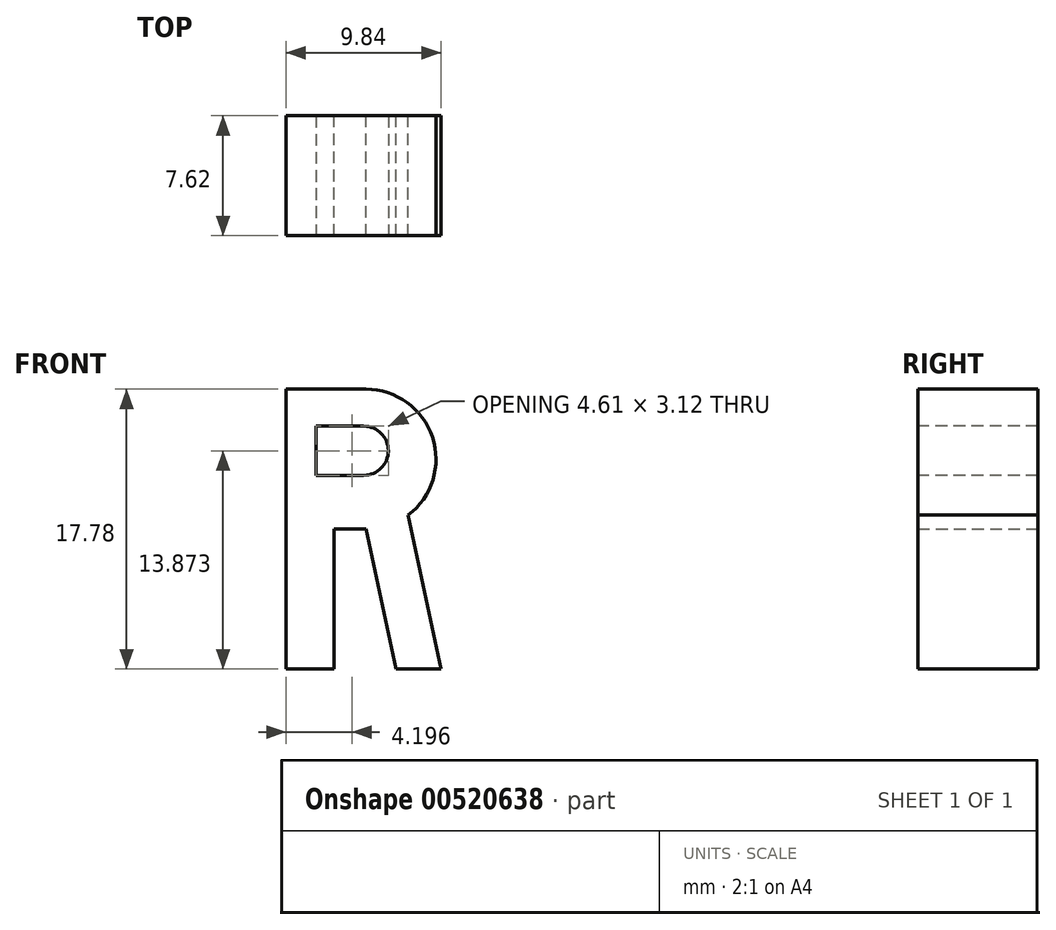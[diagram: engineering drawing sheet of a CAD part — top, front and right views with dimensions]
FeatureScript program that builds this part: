
annotation { "Feature Type Name" : "Feature", "Feature Type Description" : "" }
export const myFeature = defineFeature(function(context is Context, id is Id, definition is map)
    precondition{}
    {
        {
            var Q0;
            Q0=qCreatedBy(makeId("Front.planeOp"),FACE);
            var sketch = newSketch(context, id + "F0", { "sketchPlane" : qUnion([Q0])});
            skLineSegment(sketch, "E0.bottom", {"start": v(-12.04, 8.9) * mm, "end": v(-6.96, 8.9) * mm});
            skLineSegment(sketch, "E0.top", {"start": v(-12.04, 0) * mm, "end": v(-6.96, 0) * mm});
            skLineSegment(sketch, "E0.left", {"start": v(-12.04, 8.89) * mm, "end": v(-12.04, 0) * mm});
            skLineSegment(sketch, "E0.right", {"start": v(-6.96, 8.89) * mm, "end": v(-6.96, 0) * mm});
            skArc(sketch, "E1", {"start": v(-6.96, 0) * mm, "mid": v(-2.51, 4.44) * mm, "end": v(-6.96, 8.89) * mm});
            skLineSegment(sketch, "E2", {"start": v(-12.04, 0) * mm, "end": v(-12.04, -8.89) * mm});
            skLineSegment(sketch, "E3", {"start": v(-12.04, -8.89) * mm, "end": v(-9, -8.89) * mm});
            skLineSegment(sketch, "E4", {"start": v(-9, -8.9) * mm, "end": v(-9, 0) * mm});
            skPoint(sketch, "E5.endSnap0", {"position": v(-2.51, 4.45) * mm});
            skLineSegment(sketch, "E6", {"start": v(-6.96, 0) * mm, "end": v(-5.06, -8.89) * mm});
            skLineSegment(sketch, "E7", {"start": v(-5.06, -8.89) * mm, "end": v(-2.2, -8.89) * mm});
            skLineSegment(sketch, "E8", {"start": v(-2.2, -8.89) * mm, "end": v(-4.28, 0.9) * mm});
            skSolve(sketch);
        }
        {
            var Q0;
            Q0=makeQuery(id+"F0.imprint","IMPRINT",FACE,{"disambiguationData":[TD([[makeQuery(id+"F0.imprint","IMPRINT",EDGE,{"derivedFrom":sQuery(id+"F0.wireOp",EDGE,"E0.bottom")}),-1.0]])]});
            var Q1;
            Q1=makeQuery(id+"F0.imprint","IMPRINT",FACE,{"disambiguationData":[TD([[makeQuery(id+"F0.imprint","IMPRINT",EDGE,{"derivedFrom":sQuery(id+"F0.wireOp",EDGE,"E0.right")}),1.0]])]});
            var Q2;
            {var subQ2=sQuery(id+"F0.wireOp",EDGE,"p5OlRfSF-DRMH-5xbW-HlBg-Sh4KWYqeQvzk");Q2=makeQuery(id+"F0.imprint","IMPRINT",FACE,{"disambiguationData":[TD([[makeQuery(id+"F0.imprint","IMPRINT",EDGE,{"derivedFrom":subQ2}),-1.0]])]});}
            var Q3;
            {var subQ0=sQuery(id+"F0.wireOp",EDGE,"E2");Q3=makeQuery(id+"F0.imprint","IMPRINT",FACE,{"disambiguationData":[TD([[makeQuery(id+"F0.imprint","IMPRINT",EDGE,{"derivedFrom":subQ0}),1.0]])]});}
            extrude(context, id + "F1", {"entities" : qUnion([Q0, Q1, Q2, Q3]), "depth" : 7.62 * mm, "offsetDistance" : 25.4 * mm});
        }
        {
            var Q0;
            Q0 = qSketchRegion(id + "F0", true);
            extrude(context, id + "F2", {"entities" : qUnion([Q0]), "operationType" : NewBodyOperationType.ADD, "depth" : 7.62 * mm, "offsetDistance" : 25.4 * mm});
        }
        {
            var Q0;
            {var subQ0=sQuery(id+"F0.wireOp",EDGE,"E4");var subQ1=sQuery(id+"F0.wireOp",EDGE,"E3");var subQ2=sQuery(id+"F0.wireOp",EDGE,"E2");var subQ3=sQuery(id+"F0.wireOp",EDGE,"E1");var subQ4=sQuery(id+"F0.wireOp",EDGE,"E0.left");var subQ5=sQuery(id+"F0.wireOp",EDGE,"E0.top");var subQ6=sQuery(id+"F0.wireOp",EDGE,"E0.bottom");Q0=makeQuery(id+"F2.boolean.opBoolean","MERGE",FACE,{"derivedFrom":[makeQuery(id+"F1.opExtrude","CAP_FACE",FACE,{"disambiguationData":[OSD([subQ6,subQ5,subQ4,subQ3,subQ2,subQ1,subQ0])],"isStart":false}),makeQuery(id+"F2.opExtrude","CAP_FACE",FACE,{"disambiguationData":[OSD([subQ6,subQ5,subQ4,subQ3,subQ2,subQ1,subQ0,sQuery(id+"F0.wireOp",EDGE,"E6"),sQuery(id+"F0.wireOp",EDGE,"E7"),sQuery(id+"F0.wireOp",EDGE,"E8")])],"isStart":false})]});}
            var sketch = newSketch(context, id + "F3", { "sketchPlane" : qUnion([Q0])});
            skLineSegment(sketch, "E9.bottom", {"start": v(-10.15, 6.54) * mm, "end": v(-7.1, 6.54) * mm});
            skLineSegment(sketch, "E9.top", {"start": v(-10.15, 3.42) * mm, "end": v(-7.1, 3.42) * mm});
            skLineSegment(sketch, "E9.left", {"start": v(-10.15, 6.54) * mm, "end": v(-10.15, 3.42) * mm});
            skLineSegment(sketch, "E9.right", {"start": v(-7.1, 6.54) * mm, "end": v(-7.1, 3.42) * mm});
            skArc(sketch, "E10", {"start": v(-7.1, 3.42) * mm, "mid": v(-5.54, 4.98) * mm, "end": v(-7.1, 6.54) * mm});
            skSolve(sketch);
        }
        {
            var Q0;
            Q0 = qSketchRegion(id + "F3", true);
            extrude(context, id + "F4", {"entities" : qUnion([Q0]), "operationType" : NewBodyOperationType.REMOVE, "oppositeDirection" : true, "depth" : 25.4 * mm, "offsetDistance" : 25.4 * mm});
        }
    });
